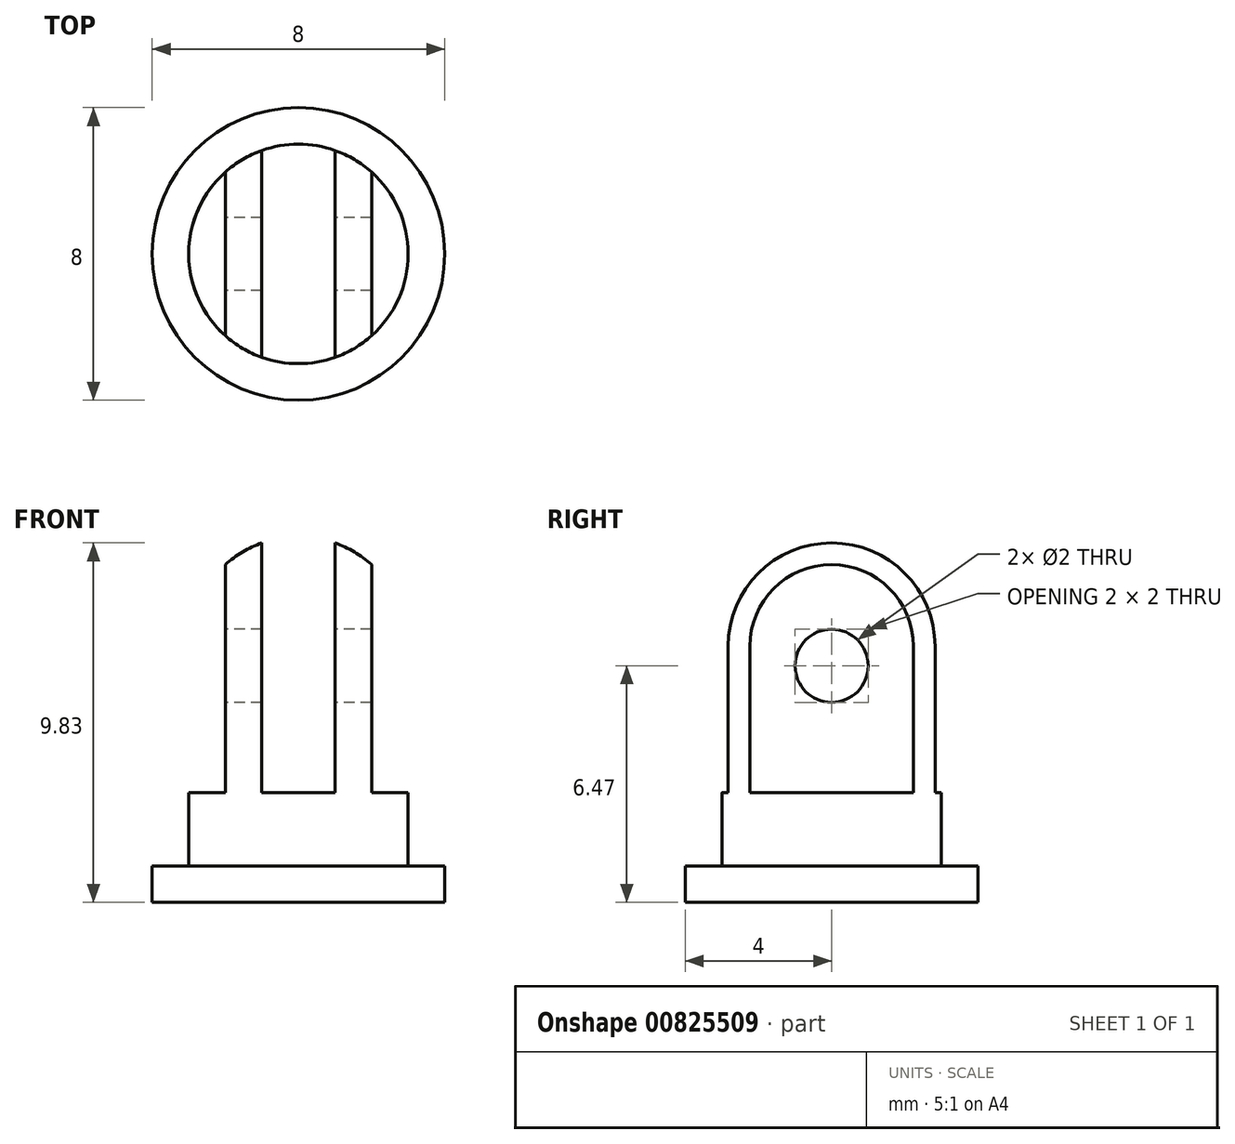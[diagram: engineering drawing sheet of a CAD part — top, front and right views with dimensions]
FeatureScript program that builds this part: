
annotation { "Feature Type Name" : "Feature", "Feature Type Description" : "" }
export const myFeature = defineFeature(function(context is Context, id is Id, definition is map)
    precondition{}
    {
        {
            var Q0;
            Q0=qCreatedBy(makeId("Top.planeOp"),FACE);
            var sketch = newSketch(context, id + "F0", { "sketchPlane" : qUnion([Q0])});
            skCircle(sketch, "E0", {"center": v(0, 0) * mm, "radius": 4 * mm});
            skSolve(sketch);
        }
        {
            var Q0;
            Q0 = qSketchRegion(id + "F0", true);
            extrude(context, id + "F1", {"entities" : qUnion([Q0]), "depth" : 1 * mm, "offsetDistance" : 25 * mm});
        }
        {
            var Q0;
            Q0=makeQuery(id+"F1.opExtrude","CAP_FACE",FACE,{"disambiguationData":[OSD([sQuery(id+"F0.wireOp",EDGE,"E0")])],"isStart":false});
            var sketch = newSketch(context, id + "F2", { "sketchPlane" : qUnion([Q0])});
            skCircle(sketch, "E1", {"center": v(0, 0) * mm, "radius": 3 * mm});
            skSolve(sketch);
        }
        {
            var Q0;
            Q0 = qSketchRegion(id + "F2", true);
            extrude(context, id + "F3", {"entities" : qUnion([Q0]), "operationType" : NewBodyOperationType.ADD, "depth" : 6 * mm, "offsetDistance" : 25 * mm});
        }
        {
            var Q0;
            Q0=makeQuery(id+"F3.opExtrude","CAP_FACE",FACE,{"disambiguationData":[OSD([sQuery(id+"F2.wireOp",EDGE,"E1")])],"isStart":false});
            var sketch = newSketch(context, id + "F4", { "sketchPlane" : qUnion([Q0])});
            skCircle(sketch, "E2", {"center": v(0, 0) * mm, "radius": 3 * mm});
            skLineSegment(sketch, "E3", {"start": v(0, 3) * mm, "end": v(0, -3) * mm});
            skSolve(sketch);
        }
        {
            var Q0;
            {var subQ0=sQuery(id+"F4.wireOp",EDGE,"E3");Q0=makeQuery(id+"F4.imprint","IMPRINT",FACE,{"disambiguationData":[TD([[makeQuery(id+"F4.imprint","IMPRINT",EDGE,{"derivedFrom":subQ0}),1.0]])]});}
            var Q1;
            Q1=sQuery(id+"F4.wireOp",EDGE,"E3");
            revolve(context, id + "F5", {"operationType" : NewBodyOperationType.ADD, "surfaceOperationType" : NewSurfaceOperationType.NEW, "entities" : qUnion([Q0]), "axis" : qUnion([Q1]), "revolveType" : RevolveType.FULL});
        }
        {
            var Q0;
            Q0=qCreatedBy(makeId("Front.planeOp"),FACE);
            var sketch = newSketch(context, id + "F6", { "sketchPlane" : qUnion([Q0])});
            skLineSegment(sketch, "E4.bottom", {"start": v(1, 3) * mm, "end": v(-1, 3) * mm});
            skLineSegment(sketch, "E4.top", {"start": v(1, 11.93) * mm, "end": v(-1, 11.93) * mm});
            skLineSegment(sketch, "E4.left", {"start": v(1, 3) * mm, "end": v(1, 11.93) * mm});
            skLineSegment(sketch, "E4.right", {"start": v(-1, 3) * mm, "end": v(-1, 11.93) * mm});
            skPoint(sketch, "E4.middle", {"position": v(0, 7.46) * mm});
            skLineSegment(sketch, "E5.bottom", {"start": v(-2, 11.93) * mm, "end": v(-4.98, 11.93) * mm});
            skLineSegment(sketch, "E5.top", {"start": v(-2, 3) * mm, "end": v(-4.98, 3) * mm});
            skLineSegment(sketch, "E5.left", {"start": v(-2, 11.93) * mm, "end": v(-2, 3) * mm});
            skLineSegment(sketch, "E5.right", {"start": v(-4.98, 11.93) * mm, "end": v(-4.98, 3) * mm});
            skLineSegment(sketch, "E6.MirrorCS", {"start": v(2, 11.93) * mm, "end": v(4.98, 11.93) * mm});
            skLineSegment(sketch, "E7.MirrorCS", {"start": v(4.98, 11.93) * mm, "end": v(4.98, 3) * mm});
            skLineSegment(sketch, "E8.MirrorCS", {"start": v(2, 3) * mm, "end": v(4.98, 3) * mm});
            skLineSegment(sketch, "E9.MirrorCS", {"start": v(2, 11.93) * mm, "end": v(2, 3) * mm});
            skSolve(sketch);
        }
        {
            var Q0;
            Q0 = qSketchRegion(id + "F6", true);
            extrude(context, id + "F7", {"entities" : qUnion([Q0]), "operationType" : NewBodyOperationType.REMOVE, "endBound" : BoundingType.SYMMETRIC, "oppositeDirection" : true, "depth" : 25 * mm, "offsetDistance" : 25 * mm});
        }
        {
            var Q0;
            Q0=makeQuery(id+"F7.boolean.opBoolean","COPY",FACE,{"derivedFrom":makeQuery(id+"F7.opExtrude","SWEPT_FACE",FACE,{"disambiguationData":[OSD([sQuery(id+"F6.wireOp",EDGE,"E5.left")])]})});
            var sketch = newSketch(context, id + "F8", { "sketchPlane" : qUnion([Q0])});
            skCircle(sketch, "E10", {"center": v(0, 6.47) * mm, "radius": 1 * mm});
            skSolve(sketch);
        }
        {
            var Q0;
            Q0 = qSketchRegion(id + "F8", true);
            extrude(context, id + "F9", {"entities" : qUnion([Q0]), "operationType" : NewBodyOperationType.REMOVE, "endBound" : BoundingType.THROUGH_ALL, "oppositeDirection" : true, "depth" : 20.9 * mm, "offsetDistance" : 25 * mm});
        }
    });
